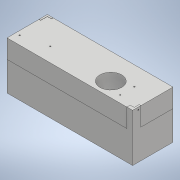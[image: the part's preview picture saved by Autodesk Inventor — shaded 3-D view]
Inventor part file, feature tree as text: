
AUTODESK INVENTOR PART (.ipt)
format: ipt  version: 2020 (Build 240168000, 168)  size: 380,928 bytes
history: native  units: mm
features: sketch x17, other x13, extrude x11, hole x5
ambient origin geometry x8: Origin, YZ Plane, XZ Plane, XY Plane, X Axis, Y Axis, Z Axis, Center Point
bodies: Body1 (feature_tree), Body2 (feature_tree)
feature tree (46):
  other  "Твердое тело1"
  extrude  "Выдавливание1"  Depth=152.5mm
  extrude  "Выдавливание2"  Depth=49.0mm
  extrude  "Выдавливание4"  Depth=30.0mm TaperAngle=0.0deg
  extrude  "Выдавливание7"  Depth=27.0mm
  extrude  "Выдавливание8"  Depth=3.0mm TaperAngle=0.0deg
  extrude  "Выдавливание9"  Depth=2.0mm
  other  "РабПлоскость1"
  other  "Разделение1"
  extrude  "Выдавливание26"  Depth=20.0mm
  extrude  "Выдавливание27"  Depth=3.0mm TaperAngle=0.0deg
  extrude  "Выдавливание28"  Depth=26.5mm
  sketch  "Эскиз24"
  hole  "Отверстие1"  [1 undecoded]
  extrude  "Выдавливание29"  Depth=25.0mm TaperAngle=0.0deg
  hole  "Отверстие2"  [1 undecoded]
  hole  "Отверстие3"  [1 undecoded]
  extrude  "Выдавливание30"  Depth=17.15mm TaperAngle=0.0deg
  hole  "Отверстие4"  [1 undecoded]
  hole  "Отверстие5"  [1 undecoded]
  sketch  "Эскиз1"
  sketch  "Эскиз2"
  sketch  "Эскиз3"
  sketch  "Эскиз4"
  sketch  "Эскиз6"
  sketch  "Эскиз7"
  sketch  "Эскиз20"
  sketch  "Эскиз21"
  sketch  "Эскиз22"
  sketch  "Эскиз23"
  sketch  "Эскиз25"
  sketch  "Эскиз26"
  sketch  "Эскиз27"
  sketch  "Эскиз28"
  sketch  "Эскиз29"
  sketch  "Эскиз30"
  other  "Проецирование ребер1"
  other  "Проецирование ребер3"
  other  "Твердое тело2"
  other  "Твердое тело3"
  other  "Проецирование ребер7"
  other  "Проецирование ребер8"
  other  "Проецирование ребер9"
  other  "Проецирование ребер10"
  other  "Проецирование ребер11"
  other  "Проецирование ребер12"
note: 5 required parameter values undecoded (feature->parameter linkage not recoverable at this tier; creation-order binding heuristic only, values carry confidence <= 0.55)
